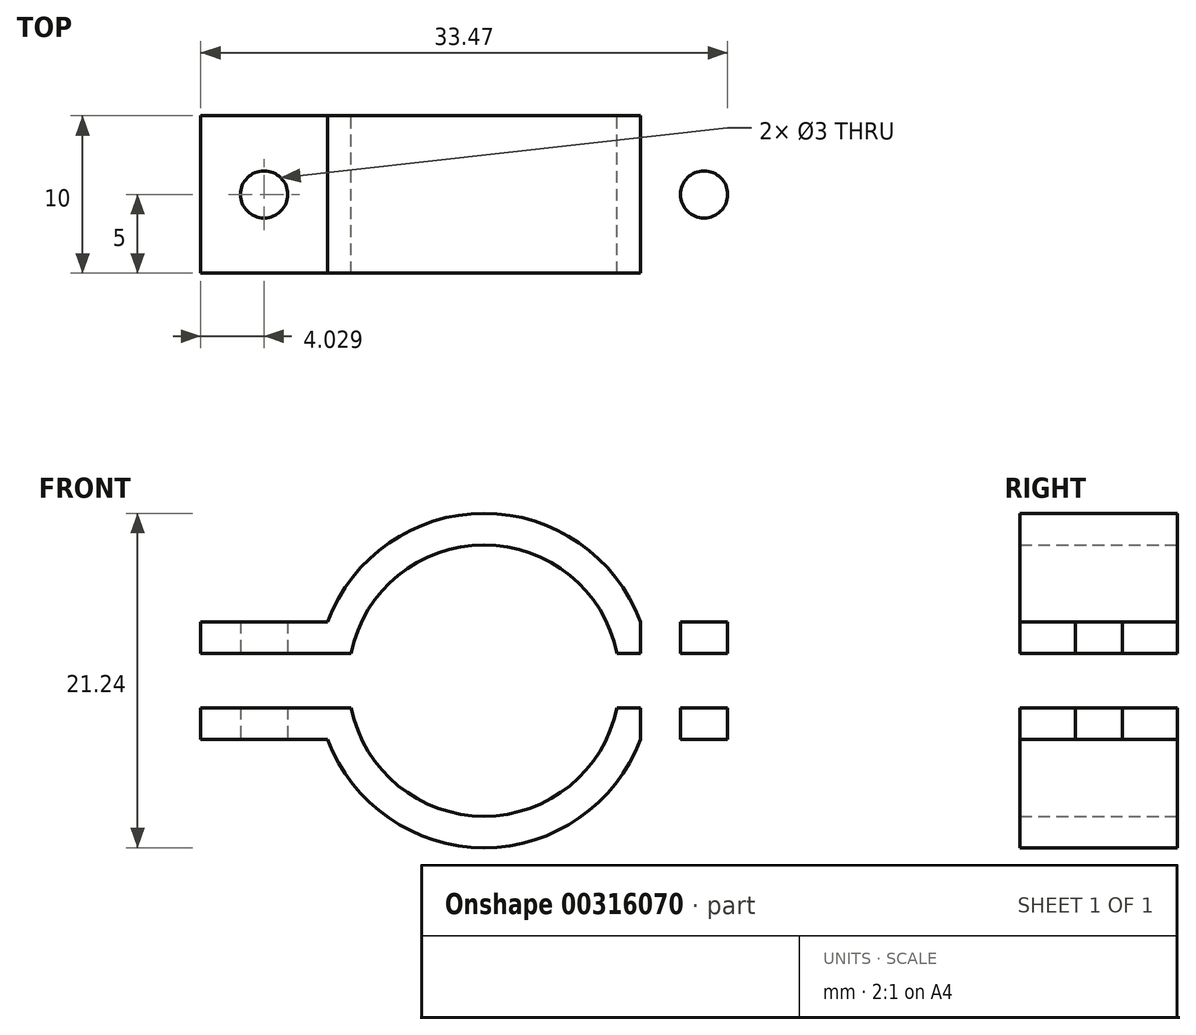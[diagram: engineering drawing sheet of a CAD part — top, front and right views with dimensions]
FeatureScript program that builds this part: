
annotation { "Feature Type Name" : "Feature", "Feature Type Description" : "" }
export const myFeature = defineFeature(function(context is Context, id is Id, definition is map)
    precondition{}
    {
        {
            var Q0;
            Q0=qCreatedBy(makeId("Front.planeOp"),FACE);
            var sketch = newSketch(context, id + "F0", { "sketchPlane" : qUnion([Q0])});
            skArc(sketch, "E0", {"start": v(-7.53, 25.16) * mm, "mid": v(0, 18.73) * mm, "end": v(7.53, 25.16) * mm, "construction": true});
            skArc(sketch, "E1.0", {"start": v(-8.44, 24.62) * mm, "mid": v(0, 17.73) * mm, "end": v(8.44, 24.62) * mm});
            skArc(sketch, "E2.trimOffspring", {"start": v(7.53, 25.16) * mm, "mid": v(0, 33.97) * mm, "end": v(-7.53, 25.16) * mm, "construction": true});
            skArc(sketch, "E3.trimOffspring", {"start": v(8.44, 28.08) * mm, "mid": v(0, 34.97) * mm, "end": v(-8.44, 28.08) * mm});
            skArc(sketch, "E4", {"start": v(-10.48, 24.62) * mm, "mid": v(0, 15.73) * mm, "end": v(10.48, 24.62) * mm});
            skLineSegment(sketch, "E5.bottom", {"start": v(18, 28.08) * mm, "end": v(7.42, 28.08) * mm});
            skLineSegment(sketch, "E5.top", {"start": v(18, 24.62) * mm, "end": v(7.42, 24.62) * mm});
            skLineSegment(sketch, "E6.bottom", {"start": v(18, 30.08) * mm, "end": v(6.64, 30.08) * mm});
            skLineSegment(sketch, "E6.top", {"start": v(18, 22.62) * mm, "end": v(6.64, 22.62) * mm});
            skLineSegment(sketch, "E6.left", {"start": v(18, 30.08) * mm, "end": v(18, 28.08) * mm});
            skLineSegment(sketch, "E6.right", {"start": v(-18, 30.08) * mm, "end": v(-18, 28.08) * mm});
            skLineSegment(sketch, "E7.trimOffspring", {"start": v(-18, 24.62) * mm, "end": v(-18, 22.62) * mm});
            skLineSegment(sketch, "E8.trimOffspring", {"start": v(18, 24.62) * mm, "end": v(18, 22.62) * mm});
            skArc(sketch, "E9.trimOffspring", {"start": v(10.48, 28.08) * mm, "mid": v(0, 36.97) * mm, "end": v(-10.48, 28.08) * mm});
            skLineSegment(sketch, "E10.trimOffspring", {"start": v(-7.42, 28.08) * mm, "end": v(-18, 28.08) * mm});
            skLineSegment(sketch, "E11.trimOffspring", {"start": v(-7.42, 24.62) * mm, "end": v(-18, 24.62) * mm});
            skLineSegment(sketch, "E12.trimOffspring", {"start": v(-6.64, 22.62) * mm, "end": v(-18, 22.62) * mm});
            skLineSegment(sketch, "E13.trimOffspring", {"start": v(-6.64, 30.08) * mm, "end": v(-18, 30.08) * mm});
            skSolve(sketch);
        }
        {
            var Q0;
            Q0=qSketchRegion(id+"F0",true);
            extrude(context, id + "F1", {"entities" : qUnion([Q0]), "depth" : 10 * mm});
        }
        {
            var Q0;
            Q0=makeQuery(id+"F1.opExtrude","SWEPT_FACE",FACE,{"disambiguationData":[OSD([sQuery(id+"F0.wireOp",EDGE,"E6.top")])]});
            var sketch = newSketch(context, id + "F2", { "sketchPlane" : qUnion([Q0])});
            skCircle(sketch, "E14", {"center": v(-13.97, 5) * mm, "radius": 1.5 * mm});
            skPoint(sketch, "E14.centerSnap0", {"position": v(-18, 5) * mm});
            skPoint(sketch, "E14.centerSnap1", {"position": v(-13.97, 10) * mm});
            skCircle(sketch, "E15.MirrorC", {"center": v(13.97, 5) * mm, "radius": 1.5 * mm});
            skSolve(sketch);
        }
        {
            var Q0;
            Q0=makeQuery(id+"F2.imprint","IMPRINT",FACE,{"disambiguationData":[TD([[makeQuery(id+"F2.imprint","IMPRINT",EDGE,{"derivedFrom":sQuery(id+"F2.wireOp",EDGE,"E14")}),1.0]])]});
            var Q1;
            Q1=makeQuery(id+"F2.imprint","IMPRINT",FACE,{"disambiguationData":[TD([[makeQuery(id+"F2.imprint","IMPRINT",EDGE,{"derivedFrom":sQuery(id+"F2.wireOp",EDGE,"E15.MirrorC")}),-1.0]])]});
            extrude(context, id + "F3", {"entities" : qUnion([Q0, Q1]), "operationType" : NewBodyOperationType.REMOVE, "oppositeDirection" : true, "depth" : 25 * mm});
        }
    });
